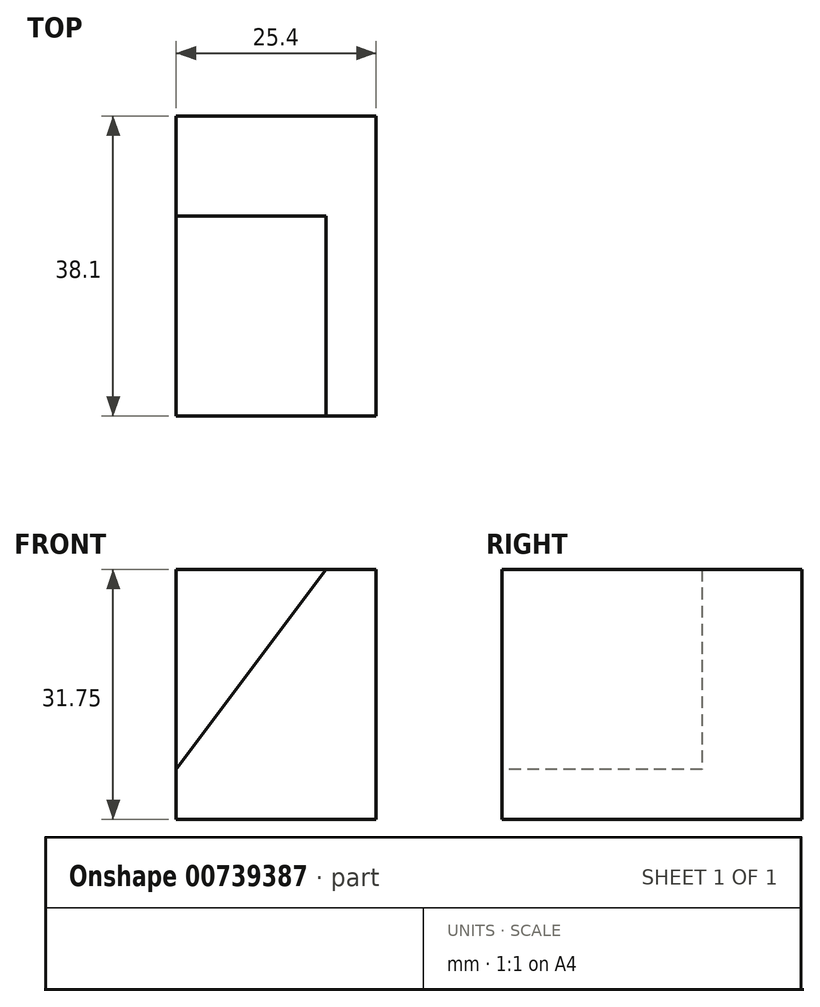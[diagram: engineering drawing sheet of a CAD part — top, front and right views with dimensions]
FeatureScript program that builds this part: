
annotation { "Feature Type Name" : "Feature", "Feature Type Description" : "" }
export const myFeature = defineFeature(function(context is Context, id is Id, definition is map)
    precondition{}
    {
        {
            var Q0;
            Q0=qCreatedBy(makeId("Front.planeOp"),FACE);
            var sketch = newSketch(context, id + "F0", { "sketchPlane" : qUnion([Q0])});
            skLineSegment(sketch, "E0", {"start": v(0, 0) * mm, "end": v(25.4, 0) * mm});
            skLineSegment(sketch, "E1", {"start": v(25.4, 0) * mm, "end": v(25.4, 31.75) * mm});
            skLineSegment(sketch, "E2", {"start": v(25.4, 31.75) * mm, "end": v(0, 31.75) * mm});
            skLineSegment(sketch, "E3", {"start": v(0, 31.75) * mm, "end": v(0, 0) * mm});
            skSolve(sketch);
        }
        {
            var Q0;
            Q0=makeQuery(id+"F0.imprint","IMPRINT",FACE,{"disambiguationData":[TD([[makeQuery(id+"F0.imprint","IMPRINT",EDGE,{"derivedFrom":sQuery(id+"F0.wireOp",EDGE,"E0")}),1.0]])]});
            extrude(context, id + "F1", {"entities" : qUnion([Q0]), "depth" : 38.1 * mm, "offsetDistance" : 25.4 * mm});
        }
        {
            var Q0;
            Q0=makeQuery(id+"F1.opExtrude","CAP_FACE",FACE,{"disambiguationData":[OSD([sQuery(id+"F0.wireOp",EDGE,"E0"),sQuery(id+"F0.wireOp",EDGE,"E1"),sQuery(id+"F0.wireOp",EDGE,"E2"),sQuery(id+"F0.wireOp",EDGE,"E3")])],"isStart":false});
            var sketch = newSketch(context, id + "F2", { "sketchPlane" : qUnion([Q0])});
            skLineSegment(sketch, "E4", {"start": v(0, 31.75) * mm, "end": v(19.05, 31.75) * mm});
            skLineSegment(sketch, "E5", {"start": v(19.05, 31.75) * mm, "end": v(0, 6.35) * mm});
            skLineSegment(sketch, "E6", {"start": v(0, 6.35) * mm, "end": v(0, 31.75) * mm});
            skSolve(sketch);
        }
        {
            var Q0;
            Q0=makeQuery(id+"F2.imprint","IMPRINT",FACE,{"disambiguationData":[TD([[makeQuery(id+"F2.imprint","IMPRINT",EDGE,{"derivedFrom":sQuery(id+"F2.wireOp",EDGE,"E4")}),1.0]])]});
            extrude(context, id + "F3", {"entities" : qUnion([Q0]), "operationType" : NewBodyOperationType.REMOVE, "oppositeDirection" : true, "depth" : 25.4 * mm, "offsetDistance" : 25.4 * mm});
        }
    });
